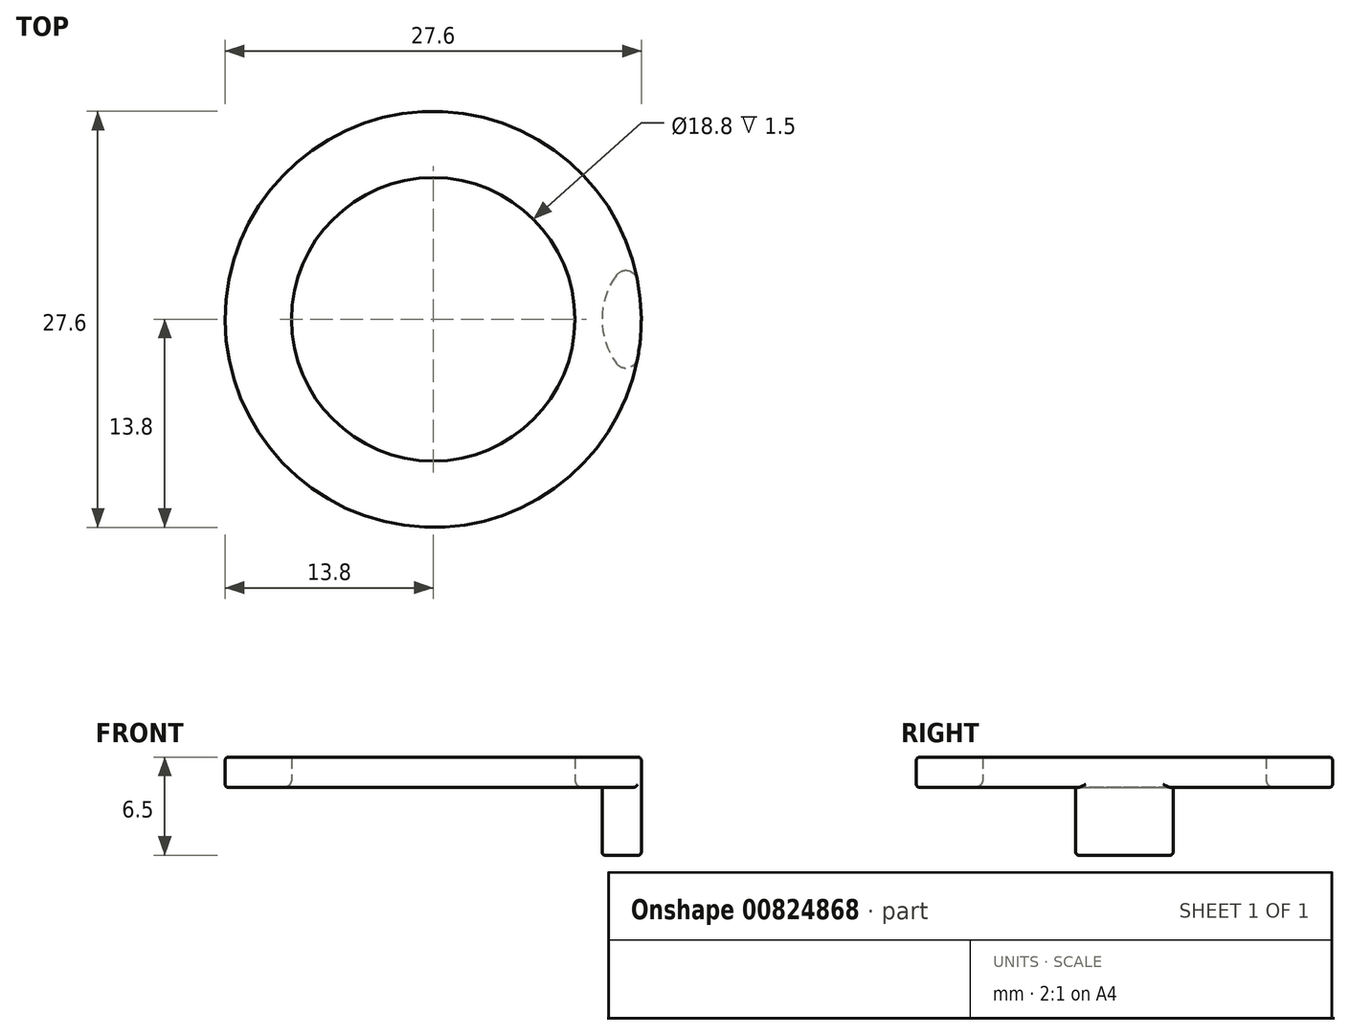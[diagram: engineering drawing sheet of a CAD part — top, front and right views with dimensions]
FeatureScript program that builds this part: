
annotation { "Feature Type Name" : "Feature", "Feature Type Description" : "" }
export const myFeature = defineFeature(function(context is Context, id is Id, definition is map)
    precondition{}
    {
        {
            var Q0;
            Q0=qCreatedBy(makeId("Top.planeOp"),FACE);
            var sketch = newSketch(context, id + "F0", { "sketchPlane" : qUnion([Q0])});
            skCircle(sketch, "E0", {"center": v(0, 0) * mm, "radius": 13.8 * mm});
            skCircle(sketch, "E1", {"center": v(0, 0) * mm, "radius": 9.4 * mm});
            skSolve(sketch);
        }
        {
            var Q0;
            Q0 = qSketchRegion(id + "F0", true);
            extrude(context, id + "F1", {"entities" : qUnion([Q0]), "depth" : 2 * mm, "offsetDistance" : 25 * mm});
        }
        {
            var Q0;
            Q0=makeQuery(id+"F1.opExtrude","CAP_EDGE",EDGE,{"disambiguationData":[OSD([sQuery(id+"F0.wireOp",EDGE,"E1")])],"isStart":true});
            fillet(context, id + "F2", {"entities" : qUnion([Q0]), "radius" : 0.5 * mm, "tangentPropagation" : true, "allowEdgeOverflow" : false});
        }
        {
            var Q0;
            Q0=makeQuery(id+"F1.opExtrude","CAP_FACE",FACE,{"disambiguationData":[OSD([sQuery(id+"F0.wireOp",EDGE,"E0"),sQuery(id+"F0.wireOp",EDGE,"E1")])],"isStart":true});
            var sketch = newSketch(context, id + "F3", { "sketchPlane" : qUnion([Q0])});
            skArc(sketch, "E2", {"start": v(12.5, 1.3) * mm, "mid": v(11.2, 0) * mm, "end": v(12.5, -1.3) * mm, "construction": true});
            skLineSegment(sketch, "E3", {"start": v(0, 0) * mm, "end": v(11.2, 0) * mm, "construction": true});
            skLineSegment(sketch, "E4", {"start": v(11.2, 0) * mm, "end": v(12.5, 0) * mm, "construction": true});
            skLineSegment(sketch, "E5", {"start": v(12.5, 0) * mm, "end": v(13.8, 0) * mm, "construction": true});
            skLineSegment(sketch, "E6", {"start": v(12.5, 1.3) * mm, "end": v(13.74, 1.3) * mm, "construction": true});
            skLineSegment(sketch, "E7", {"start": v(12.5, -1.3) * mm, "end": v(13.74, -1.3) * mm, "construction": true});
            skArc(sketch, "E8", {"start": v(13.74, -1.3) * mm, "mid": v(13.8, 0) * mm, "end": v(13.74, 1.3) * mm, "construction": true});
            skArc(sketch, "E9", {"start": v(12.12, 2.89) * mm, "mid": v(11.2, 0) * mm, "end": v(12.12, -2.89) * mm});
            skArc(sketch, "E10", {"start": v(13.56, -2.58) * mm, "mid": v(13.8, 0) * mm, "end": v(13.56, 2.58) * mm});
            skPoint(sketch, "E11.visualSharp", {"position": v(13.2, 4) * mm});
            skArc(sketch, "E11.filletArc", {"start": v(13.56, 2.58) * mm, "mid": v(12.94, 3.2) * mm, "end": v(12.12, 2.89) * mm});
            skPoint(sketch, "E12.visualSharp", {"position": v(13.2, -4) * mm});
            skArc(sketch, "E12.filletArc", {"start": v(12.12, -2.89) * mm, "mid": v(12.94, -3.2) * mm, "end": v(13.56, -2.58) * mm});
            skSolve(sketch);
        }
        {
            var Q0;
            Q0 = qSketchRegion(id + "F3", true);
            var Q1;
            Q1=makeQuery(id+"FcnWL43BjcRguwH_1.3.F3.imprint","IMPRINT",FACE,{"disambiguationData":[TD([[makeQuery(id+"FcnWL43BjcRguwH_1.3.F3.imprint","IMPRINT",EDGE,{"derivedFrom":sQuery(id+"FcnWL43BjcRguwH_1.3.F3.wireOp",EDGE,"E2")}),1.0]])]});
            var Q2;
            Q2=makeQuery(id+"FcnWL43BjcRguwH_1.2.F3.imprint","IMPRINT",FACE,{"disambiguationData":[TD([[makeQuery(id+"FcnWL43BjcRguwH_1.2.F3.imprint","IMPRINT",EDGE,{"derivedFrom":sQuery(id+"FcnWL43BjcRguwH_1.2.F3.wireOp",EDGE,"E2")}),1.0]])]});
            var Q3;
            Q3=makeQuery(id+"FcnWL43BjcRguwH_1.1.F3.imprint","IMPRINT",FACE,{"disambiguationData":[TD([[makeQuery(id+"FcnWL43BjcRguwH_1.1.F3.imprint","IMPRINT",EDGE,{"derivedFrom":sQuery(id+"FcnWL43BjcRguwH_1.1.F3.wireOp",EDGE,"E2")}),1.0]])]});
            extrude(context, id + "F4", {"entities" : qUnion([Q0, Q1, Q2, Q3]), "operationType" : NewBodyOperationType.ADD, "depth" : 4.5 * mm, "offsetDistance" : 25 * mm});
        }
        {
            var Q0;
            Q0=makeQuery(id+"F4.opExtrude","CAP_EDGE",EDGE,{"disambiguationData":[OSD([sQuery(id+"F3.wireOp",EDGE,"E10")])],"isStart":false});
            var Q1;
            Q1=makeQuery(id+"F4.opExtrude","CAP_EDGE",EDGE,{"disambiguationData":[OSD([sQuery(id+"F3.wireOp",EDGE,"E9")])],"isStart":true});
            fillet(context, id + "F5", {"entities" : qUnion([Q0, Q1]), "radius" : 0.2 * mm, "tangentPropagation" : true, "allowEdgeOverflow" : false});
        }
        {
            var Q0;
            Q0=qCreatedBy(makeId("Front.planeOp"),FACE);
            var sketch = newSketch(context, id + "F6", { "sketchPlane" : qUnion([Q0])});
            skLineSegment(sketch, "E13", {"start": v(0, 0) * mm, "end": v(0, -11.2) * mm, "construction": true});
            skSolve(sketch);
        }
        {
            var Q0;
            Q0=makeQuery(id+"F1.opExtrude","CAP_EDGE",EDGE,{"disambiguationData":[OSD([sQuery(id+"F0.wireOp",EDGE,"E0")])],"isStart":false});
            var Q1;
            Q1=makeQuery(id+"F1.opExtrude","CAP_EDGE",EDGE,{"disambiguationData":[OSD([sQuery(id+"F0.wireOp",EDGE,"E0")])],"isStart":true});
            fillet(context, id + "F7", {"entities" : qUnion([Q0, Q1]), "radius" : 0.2 * mm, "tangentPropagation" : true, "allowEdgeOverflow" : false});
        }
    });
